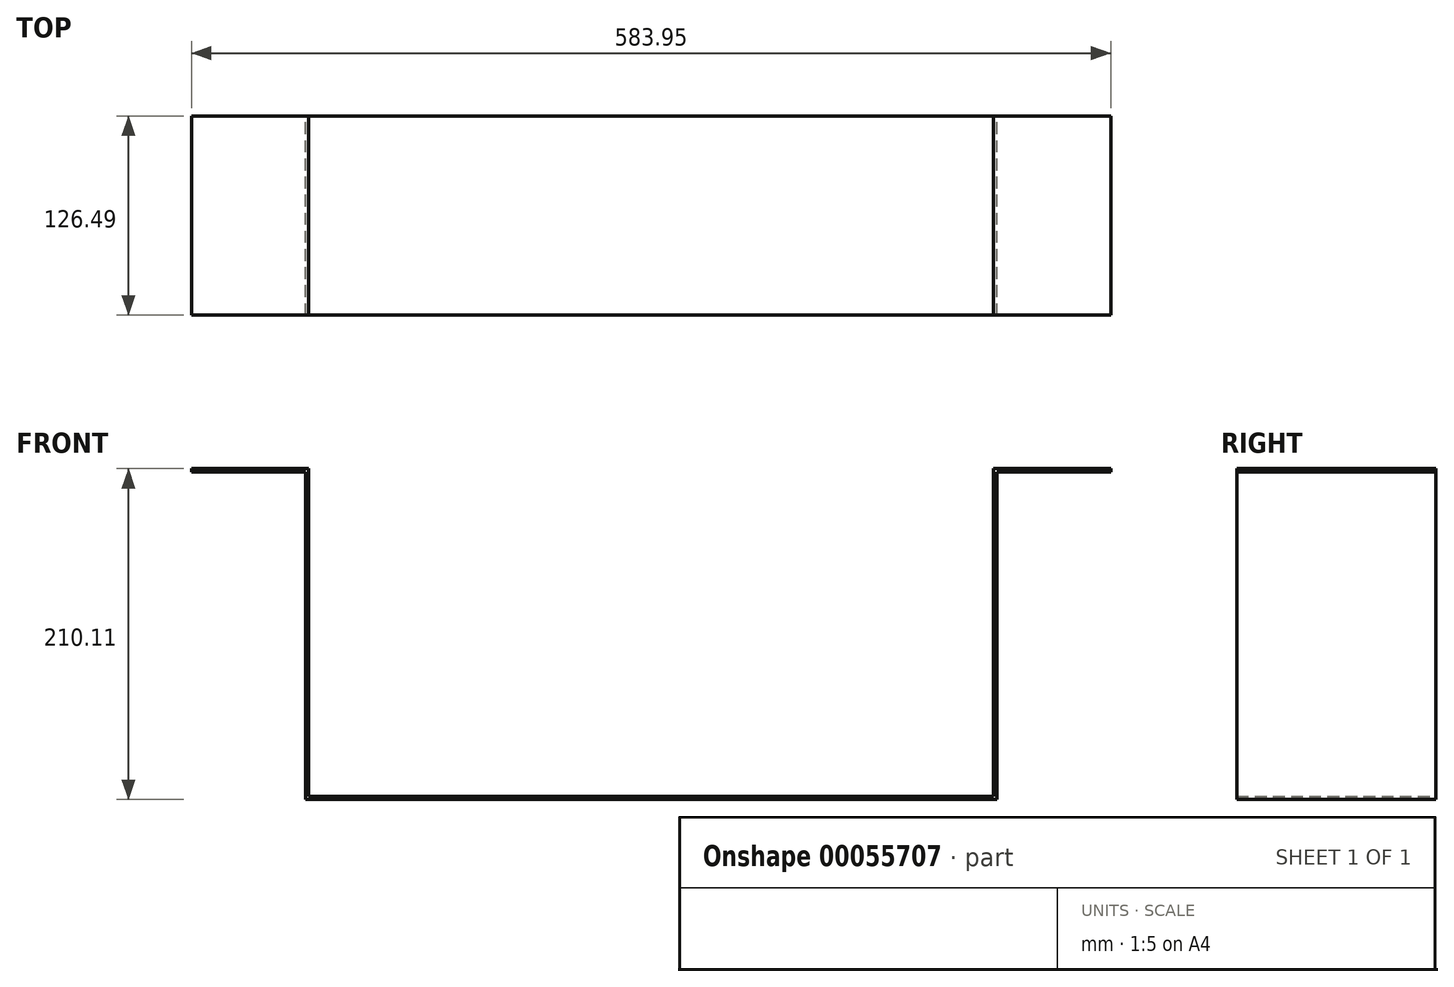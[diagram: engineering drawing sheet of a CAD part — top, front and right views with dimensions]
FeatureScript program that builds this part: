
annotation { "Feature Type Name" : "Feature", "Feature Type Description" : "" }
export const myFeature = defineFeature(function(context is Context, id is Id, definition is map)
    precondition{}
    {
        {
            var Q0;
            Q0=qCreatedBy(makeId("Front.planeOp"),FACE);
            var sketch = newSketch(context, id + "F0", { "sketchPlane" : qUnion([Q0])});
            skLineSegment(sketch, "E0", {"start": v(0, 0) * mm, "end": v(438.91, 0) * mm});
            skLineSegment(sketch, "E1", {"start": v(438.91, 0) * mm, "end": v(438.91, 208.08) * mm});
            skLineSegment(sketch, "E2", {"start": v(0, 0) * mm, "end": v(0, 208.08) * mm});
            skLineSegment(sketch, "E3", {"start": v(0, 208.08) * mm, "end": v(-72.52, 208.08) * mm});
            skLineSegment(sketch, "E4", {"start": v(438.91, 208.08) * mm, "end": v(511.43, 208.08) * mm});
            skLineSegment(sketch, "E5", {"start": v(-72.52, 208.08) * mm, "end": v(-72.52, 210.1) * mm});
            skLineSegment(sketch, "E6", {"start": v(-72.52, 210.1) * mm, "end": v(2.03, 210.1) * mm});
            skLineSegment(sketch, "E7", {"start": v(2.03, 210.1) * mm, "end": v(2.03, 2.03) * mm});
            skLineSegment(sketch, "E8", {"start": v(2.03, 2.03) * mm, "end": v(436.88, 2.03) * mm});
            skLineSegment(sketch, "E9", {"start": v(436.88, 2.03) * mm, "end": v(436.88, 210.1) * mm});
            skLineSegment(sketch, "E10", {"start": v(436.88, 210.1) * mm, "end": v(511.43, 210.1) * mm});
            skLineSegment(sketch, "E11", {"start": v(511.43, 210.1) * mm, "end": v(511.43, 208.08) * mm});
            skLineSegment(sketch, "E12", {"start": v(2.03, 0) * mm, "end": v(2.03, -6.02) * mm});
            skLineSegment(sketch, "E13", {"start": v(2.03, -6.02) * mm, "end": v(436.88, -6.02) * mm});
            skLineSegment(sketch, "E14", {"start": v(436.88, -6.02) * mm, "end": v(436.88, 0) * mm});
            skLineSegment(sketch, "E15", {"start": v(438.91, 2.03) * mm, "end": v(449.58, 2.03) * mm});
            skLineSegment(sketch, "E16", {"start": v(449.58, 2.03) * mm, "end": v(449.58, 178.8) * mm});
            skLineSegment(sketch, "E17", {"start": v(449.58, 178.8) * mm, "end": v(438.91, 178.8) * mm});
            skLineSegment(sketch, "E18", {"start": v(438.91, 196.98) * mm, "end": v(487.04, 197.4) * mm});
            skLineSegment(sketch, "E19", {"start": v(487.04, 197.4) * mm, "end": v(487.04, 208.08) * mm});
            skLineSegment(sketch, "E20", {"start": v(487.04, 210.1) * mm, "end": v(438.8, 210.1) * mm});
            skLineSegment(sketch, "E21", {"start": v(0, 197.4) * mm, "end": v(0, 208.08) * mm});
            skLineSegment(sketch, "E22", {"start": v(0, 197.4) * mm, "end": v(-48.13, 197.4) * mm});
            skLineSegment(sketch, "E23", {"start": v(-48.13, 197.4) * mm, "end": v(-48.13, 208.08) * mm});
            skSolve(sketch);
        }
        {
            var Q0;
            {var subQ0=sQuery(id+"F0.wireOp",EDGE,"E2");Q0=makeQuery(id+"F0.imprint","IMPRINT",FACE,{"disambiguationData":[TD([[makeQuery(id+"F0.imprint","IMPRINT",EDGE,{"derivedFrom":subQ0}),-1.0]])]});}
            extrude(context, id + "F1", {"entities" : qUnion([Q0]), "depth" : 126.5 * mm});
        }
    });
